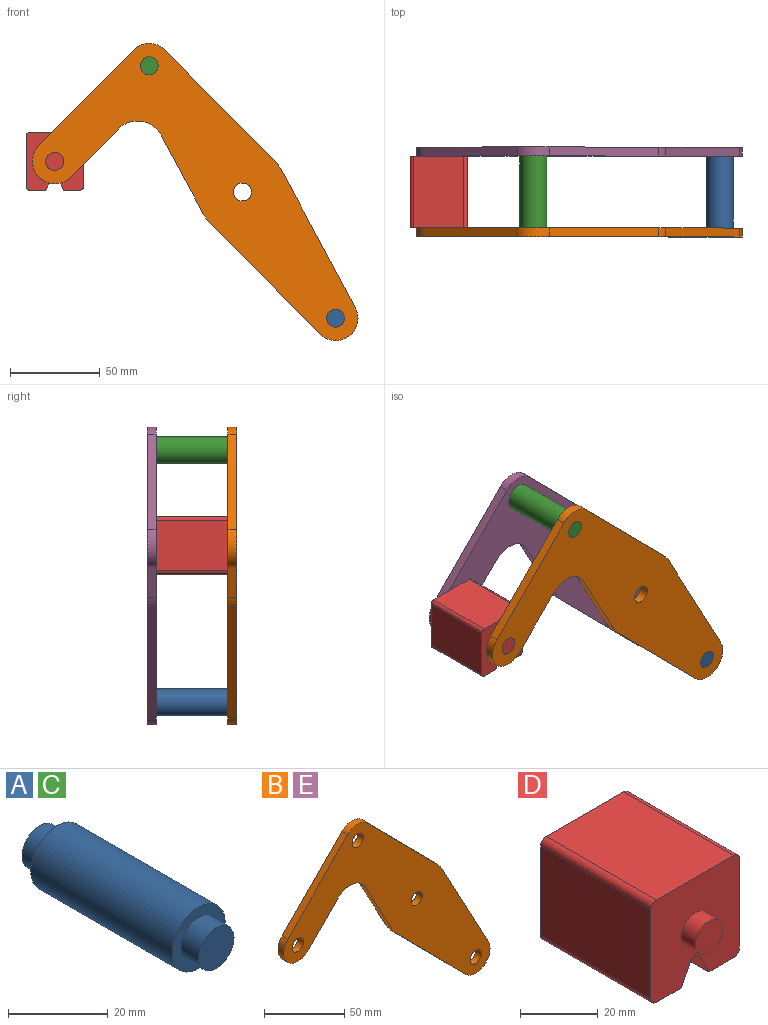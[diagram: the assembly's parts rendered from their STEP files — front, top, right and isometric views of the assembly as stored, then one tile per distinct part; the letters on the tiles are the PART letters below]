
ASSEMBLY  parts=5 mates=3
PART A: 7 faces, bbox 15x50x15 mm
  f0: cylinder r=7.5mm len=40mm, axis (0,-1,0), area 1885mm2, adj f2,f5
  f1: cylinder r=5mm len=10mm, axis (0,1,0), area 157.1mm2, adj f2,f3
  f2: plane 15x15mm, normal (0,-1,0), area 98.2mm2, adj f0,f1
  f3: plane 10x10mm, normal (0,-1,0), area 78.5mm2, adj f1
  f4: cylinder r=5mm len=10mm, axis (0,-1,0), area 157.1mm2, adj f5,f6
  f5: plane 15x15mm, normal (0,1,0), area 98.2mm2, adj f0,f4
  f6: plane 10x10mm, normal (0,1,0), area 78.5mm2, adj f4
PART B: 18 faces, bbox 181.7x5x165.8 mm
  f0: plane 43.49x23.35mm, normal (-0.88,0,-0.47), area 246.8mm2, adj f1,f14,f16,f17
  f1: cylinder r=25mm len=5.75mm, axis (0,1,0), area 35.8mm2, adj f0,f2,f16,f17
  f2: plane 61.6x60.87mm, normal (-0.71,0,-0.7), area 433mm2, adj f1,f3,f16,f17
  f3: cylinder r=12.5mm len=21.39mm, axis (0,1,0), area 178.4mm2, adj f2,f4,f16,f17
  f4: plane 76.3x40.96mm, normal (0.88,0,0.47), area 433mm2, adj f3,f5,f16,f17
  f5: cylinder r=25mm len=5.75mm, axis (0,1,0), area 35.8mm2, adj f4,f6,f16,f17
  f6: plane 61.6x60.87mm, normal (0.71,0,0.7), area 433mm2, adj f5,f7,f16,f17
  f7: cylinder r=12.5mm len=17.78mm, axis (0,1,0), area 98.9mm2, adj f6,f8,f16,f17
  f8: plane 53.35x52.71mm, normal (-0.71,0,0.7), area 375mm2, adj f7,f9,f16,f17
  f9: cylinder r=12.5mm len=21.39mm, axis (0,1,0), area 196.3mm2, adj f8,f10,f16,f17
  f10: plane 26.86x26.54mm, normal (0.71,0,-0.7), area 188.8mm2, adj f9,f14,f16,f17
  f11: cylinder r=5mm len=10mm, axis (0,1,0), area 157.1mm2, adj f16,f17
  f12: cylinder r=5mm len=10mm, axis (0,1,0), area 157.1mm2, adj f16,f17
  f13: cylinder r=5mm len=10mm, axis (0,1,0), area 157.1mm2, adj f16,f17
  f14: cylinder r=15mm len=23.89mm, axis (0,1,0), area 140.2mm2, adj f0,f10,f16,f17
  f15: cylinder r=5mm len=10mm, axis (0,1,0), area 157.1mm2, adj f16,f17
  f16: plane 181.66x165.78mm, normal (0,-1,0), area 8710.1mm2, adj f0,f1,f2,f3,f4,f5,f6,f7
  f17: plane 181.66x165.78mm, normal (0,1,0), area 8710.1mm2, adj f0,f1,f2,f3,f4,f5,f6,f7
PART C: same geometry as A
PART D: 18 faces, bbox 32.1x50x32.1 mm
  f0: plane 40x28.08mm, normal (1,0,0), area 1123.1mm2, adj f4,f10,f13,f14
  f1: plane 40x9.04mm, normal (0,0,-1), area 361.6mm2, adj f2,f4,f10,f14
  f2: plane 40x6.42mm, normal (-0.89,0,-0.45), area 287.2mm2, adj f1,f4,f10,f15
  f3: plane 40x6.42mm, normal (0.89,0,-0.45), area 287.2mm2, adj f4,f5,f10,f15
  f4: plane 32.08x32.08mm, normal (0,-1,0), area 900.6mm2, adj f0,f1,f2,f3,f5,f6,f7,f9
  f5: plane 40x9.04mm, normal (0,0,-1), area 361.6mm2, adj f3,f4,f10,f16
  f6: plane 40x28.08mm, normal (0,0,1), area 1123.1mm2, adj f4,f10,f13,f17
  f7: plane 40x28.08mm, normal (-1,0,0), area 1123.1mm2, adj f4,f10,f16,f17
  f8: plane 10x10mm, normal (0,-1,0), area 78.5mm2, adj f9
  f9: cylinder r=5mm len=10mm, axis (0,1,0), area 157.1mm2, adj f4,f8
  f10: plane 32.08x32.08mm, normal (0,1,0), area 900.6mm2, adj f0,f1,f2,f3,f5,f6,f7,f12
  f11: plane 10x10mm, normal (0,1,0), area 78.5mm2, adj f12
  f12: cylinder r=5mm len=10mm, axis (0,-1,0), area 157.1mm2, adj f10,f11
  f13: cylinder r=2mm len=40mm, axis (0,1,0), area 125.7mm2, adj f0,f4,f6,f10
  f14: cylinder r=2mm len=40mm, axis (0,-1,0), area 125.7mm2, adj f0,f1,f4,f10
  f15: cylinder r=2mm len=40mm, axis (0,1,0), area 177.1mm2, adj f2,f3,f4,f10
  f16: cylinder r=2mm len=40mm, axis (0,1,0), area 125.7mm2, adj f4,f5,f7,f10
  f17: cylinder r=2mm len=40mm, axis (0,-1,0), area 125.7mm2, adj f4,f6,f7,f10
PART E: same geometry as B
PLACE A t=(103.95,-20,-140.78)mm
PLACE B t=(0,-20,0)mm fixed
PLACE C t=(0,-20,0)mm
PLACE D t=(0,-20,0)mm
PLACE E t=(0,25,0)mm
MATE fastened E.f7 <-> C.f0  axis (0,-1,0) through (-51.98,20,70.39)mm
MATE revolute B.f9 <-> D.f9  axis (0,1,0) through (-104.69,-20,17.04)mm
MATE fastened B.f3 <-> A.f0  axis (0,1,0) through (51.98,-20,-70.39)mm
